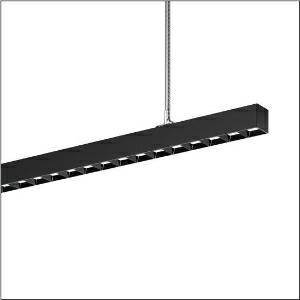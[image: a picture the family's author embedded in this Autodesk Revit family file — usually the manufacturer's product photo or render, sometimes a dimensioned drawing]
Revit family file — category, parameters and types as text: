
# Revit family: silica_r__21_51mx32dc4dbb_b922
name_source: partatom
category: Lighting Fixtures
units: mm (PartAtom-declared; Revit-internal decimal feet)

## family parameters
Cut with Voids When Loaded = No
Host = Face
Light Source = No
Part Type = Normal
Room Calculation Point = No
Round Connector Dimension = Use Diameter
Shared = No

## types (1)
- --- (1 x LED, 18230 lm, 105.8 W, 4000K)
    Apparent Load = 106 VA
    CIE Flux Codes = 86 99 100 59 100
    Color Rendering = 80
    Color Temperature = 4000K
    Default Elevation = 1800 mm
    Description = Silica® 21, office luminaire, primary light control with darklight reflector, of PMMA, black, CAT 2 (L<= 3000cd/m²), light emission: direct/indirect distribution, primary light characteristic: symmetric, installation type: suspended mounting, LED, rated luminous flux: 18.230lm, luminous efficacy: 172lm/W, light colour: 840, colour temperature: 4000K, with terminal, 3+2-pole, max. 2.5mm², mains connection: 220..240V, AC, 50/60Hz, rated input power: 105.8W, luminaire housing, of aluminium, jet black (RAL 9005), length: 3.004mm, width: 53mm, height: 53mm, protection rating (complete): IP20, insulation class (complete): insulation class I (protective earthing), certification: CE, permissible operating ambient temperature: 0..+35°C, standard: EN 50419, packaging unit: 1 piece
    Height = 53 mm
    Lamp = 1 x LED
    Lamp Light Flux = 18230 lm
    Lamp Power = 105.8 W
    Lamp count = 1
    Length = 3004 mm
    Luminous efficacy = 172 lm/W
    Manufacturer = Siteco
    ModVariant = No
    Model = 51MX32DC4DBB
    Mounting Place = Ceiling
    Mounting Type = Pendant
    Number of Poles = 1
    OnlyDefault = Yes
    Power Factor = 1
    Product Name = Silica® 21
    Product group = office luminaire | ceiling pendant
    ProductGroupID = 905
    Protection Class = Protection class I
    Protection Degree = IP 20
    RLX_Detail_Level = 1
    RlxData = <blob elided: 68661 chars, md5=4ba6fa05>
    Socket = socket
    Standby Power = 0 W
    System Light Flux = 18230 lm
    System Power = 106 W
    Type Comments = factory setting: luminous flux: 100 % | dim-lin: 254 | 366 mA
    Type Image = l_1251718.jpg
    URL = http://relux.com
    VarID = @adj_031295
    Voltage = 0 V
    Weight = 0.00 kg
    Width = 53 mm

## geometry (parser evidence)
native form markers: Blend x4, Sweep x12
no freeform markers — native parametric forms only
